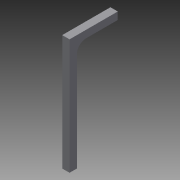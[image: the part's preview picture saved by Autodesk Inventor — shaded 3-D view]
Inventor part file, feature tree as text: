
AUTODESK INVENTOR PART (.ipt)
format: ipt  version: 2015 (Build 190159000, 159)  size: 72,704 bytes
history: native  units: in
note: dims shown in document units (in); Inventor stores cm internally (conversion verified against a paired STEP export)
features: extrude x1, sketch x1
ambient origin geometry x8: Origin, YZ Plane, XZ Plane, XY Plane, X Axis, Y Axis, Z Axis, Center Point
bodies: Solid1 (feature_tree)
feature tree (2):
  extrude  "Extrusion1"  Depth=0.125in
  sketch  "Sketch1"  dims[d0=0.1in d1=0.125in d2=0.1in d3=0.0in]
